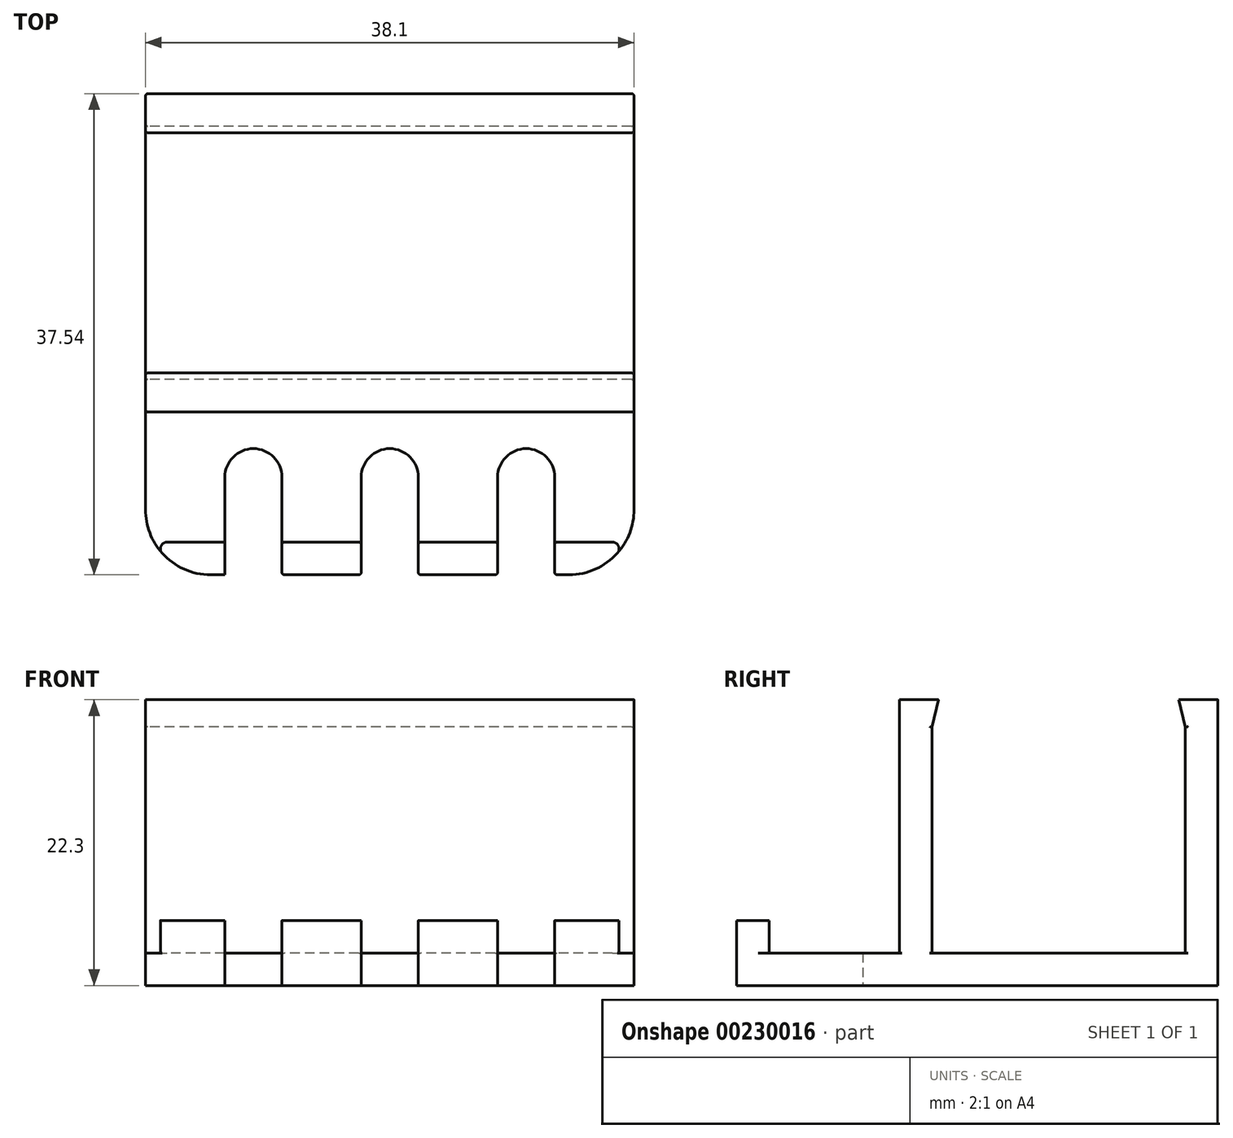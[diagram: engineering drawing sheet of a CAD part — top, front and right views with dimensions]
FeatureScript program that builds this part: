
annotation { "Feature Type Name" : "Feature", "Feature Type Description" : "" }
export const myFeature = defineFeature(function(context is Context, id is Id, definition is map)
    precondition{}
    {
        {
            var Q0;
            Q0=qCreatedBy(makeId("Right.planeOp"),FACE);
            var sketch = newSketch(context, id + "F0", { "sketchPlane" : qUnion([Q0])});
            skLineSegment(sketch, "E0.bottom", {"start": v(0, 0) * mm, "end": v(2.54, 0) * mm});
            skLineSegment(sketch, "E0.top", {"start": v(0, 22.3) * mm, "end": v(2.54, 22.3) * mm});
            skLineSegment(sketch, "E0.left", {"start": v(0, 2.54) * mm, "end": v(0, 22.3) * mm});
            skLineSegment(sketch, "E0.right", {"start": v(2.54, 2.54) * mm, "end": v(2.54, 22.3) * mm});
            skLineSegment(sketch, "E1.bottom", {"start": v(2.54, 0) * mm, "end": v(24.84, 0) * mm});
            skLineSegment(sketch, "E1.top", {"start": v(2.54, 2.54) * mm, "end": v(22.3, 2.54) * mm});
            skLineSegment(sketch, "E2.top", {"start": v(24.84, 22.3) * mm, "end": v(22.3, 22.3) * mm});
            skLineSegment(sketch, "E2.left", {"start": v(24.84, 2.54) * mm, "end": v(24.84, 22.3) * mm});
            skLineSegment(sketch, "E2.right", {"start": v(22.3, 2.54) * mm, "end": v(22.3, 20.17) * mm});
            skLineSegment(sketch, "E3.bottom", {"start": v(0, 2.54) * mm, "end": v(-12.7, 2.54) * mm});
            skLineSegment(sketch, "E3.top", {"start": v(0, 0) * mm, "end": v(-12.7, 0) * mm});
            skLineSegment(sketch, "E3.right", {"start": v(-12.7, 2.54) * mm, "end": v(-12.7, 0) * mm});
            skLineSegment(sketch, "E4", {"start": v(24.84, 2.54) * mm, "end": v(24.84, 0) * mm});
            skLineSegment(sketch, "E5", {"start": v(22.3, 20.17) * mm, "end": v(21.8, 22.3) * mm});
            skLineSegment(sketch, "E6", {"start": v(21.8, 22.3) * mm, "end": v(22.3, 22.3) * mm});
            skLineSegment(sketch, "E7", {"start": v(12.42, 2.54) * mm, "end": v(12.42, 18.7) * mm, "construction": true});
            skLineSegment(sketch, "E8.MirrorCS", {"start": v(2.54, 20.17) * mm, "end": v(3.05, 22.3) * mm});
            skLineSegment(sketch, "E9.MirrorCS", {"start": v(3.05, 22.3) * mm, "end": v(2.54, 22.3) * mm});
            skLineSegment(sketch, "E10.bottom", {"start": v(-12.7, 2.54) * mm, "end": v(-10.16, 2.54) * mm});
            skLineSegment(sketch, "E10.top", {"start": v(-12.7, 5.08) * mm, "end": v(-10.16, 5.08) * mm});
            skLineSegment(sketch, "E10.left", {"start": v(-12.7, 2.54) * mm, "end": v(-12.7, 5.08) * mm});
            skLineSegment(sketch, "E10.right", {"start": v(-10.16, 2.54) * mm, "end": v(-10.16, 5.08) * mm});
            skSolve(sketch);
        }
        {
            var Q0;
            Q0 = qSketchRegion(id + "F0", true);
            extrude(context, id + "F1", {"entities" : qUnion([Q0]), "endBound" : BoundingType.SYMMETRIC, "depth" : 38.1 * mm});
        }
        {
            var Q0;
            Q0=makeQuery(id+"F1.opExtrude","SWEPT_FACE",FACE,{"disambiguationData":[OSD([sQuery(id+"F0.wireOp",EDGE,"E3.bottom")])]});
            var sketch = newSketch(context, id + "F2", { "sketchPlane" : qUnion([Q0])});
            skLineSegment(sketch, "E11", {"start": v(-19.05, -5.08) * mm, "end": v(-12.86, -5.08) * mm, "construction": true});
            skArc(sketch, "E12", {"start": v(2.22, -5.08) * mm, "mid": v(0, -2.86) * mm, "end": v(-2.22, -5.08) * mm});
            skArc(sketch, "E13", {"start": v(12.86, -5.08) * mm, "mid": v(10.64, -2.86) * mm, "end": v(8.41, -5.08) * mm});
            skArc(sketch, "E14", {"start": v(-8.41, -5.08) * mm, "mid": v(-10.64, -2.86) * mm, "end": v(-12.86, -5.08) * mm});
            skLineSegment(sketch, "E15.top", {"start": v(-12.86, -12.7) * mm, "end": v(-8.41, -12.7) * mm});
            skLineSegment(sketch, "E15.left", {"start": v(-12.86, -5.08) * mm, "end": v(-12.86, -12.7) * mm});
            skLineSegment(sketch, "E15.right", {"start": v(-8.41, -5.08) * mm, "end": v(-8.41, -12.7) * mm});
            skLineSegment(sketch, "E16.top", {"start": v(-2.22, -12.7) * mm, "end": v(2.22, -12.7) * mm});
            skLineSegment(sketch, "E16.left", {"start": v(-2.22, -5.08) * mm, "end": v(-2.22, -12.7) * mm});
            skLineSegment(sketch, "E16.right", {"start": v(2.22, -5.08) * mm, "end": v(2.22, -12.7) * mm});
            skLineSegment(sketch, "E17.top", {"start": v(8.41, -12.7) * mm, "end": v(12.86, -12.7) * mm});
            skLineSegment(sketch, "E17.left", {"start": v(8.41, -5.08) * mm, "end": v(8.41, -12.7) * mm});
            skLineSegment(sketch, "E17.right", {"start": v(12.86, -5.08) * mm, "end": v(12.86, -12.7) * mm});
            skLineSegment(sketch, "E18.trimOffspring", {"start": v(-8.41, -5.08) * mm, "end": v(-2.22, -5.08) * mm, "construction": true});
            skLineSegment(sketch, "E19.trimOffspring", {"start": v(2.22, -5.08) * mm, "end": v(8.41, -5.08) * mm, "construction": true});
            skLineSegment(sketch, "E20.trimOffspring", {"start": v(12.86, -5.08) * mm, "end": v(19.05, -5.08) * mm, "construction": true});
            skSolve(sketch);
        }
        {
            var Q0;
            Q0 = qSketchRegion(id + "F2", true);
            extrude(context, id + "F3", {"entities" : qUnion([Q0]), "operationType" : NewBodyOperationType.REMOVE, "endBound" : BoundingType.SYMMETRIC, "depth" : 25.4 * mm});
        }
        {
            var Q0;
            Q0=makeQuery(id+"F1.opExtrude","CAP_EDGE",EDGE,{"disambiguationData":[OSD([sQuery(id+"F0.wireOp",EDGE,"E3.right"),sQuery(id+"F0.wireOp",EDGE,"E10.left")])],"isStart":false});
            var Q1;
            Q1=makeQuery(id+"F1.opExtrude","CAP_EDGE",EDGE,{"disambiguationData":[OSD([sQuery(id+"F0.wireOp",EDGE,"E3.right"),sQuery(id+"F0.wireOp",EDGE,"E10.left")])],"isStart":true});
            fillet(context, id + "F4", {"entities" : qUnion([Q0, Q1]), "radius" : 5.08 * mm, "tangentPropagation" : true, "allowEdgeOverflow" : false});
        }
        {
            var Q0;
            {var subQ0=sQuery(id+"F0.wireOp",EDGE,"E10.right");var subQ1=sQuery(id+"F0.wireOp",EDGE,"E10.left");var subQ3=sQuery(id+"F0.wireOp",EDGE,"E3.right");Q0=makeQuery(id+"F4.opFillet","BLEND_EDGE",EDGE,{"blendedFrom":[makeQuery(id+"F1.opExtrude","CAP_EDGE",EDGE,{"disambiguationData":[OSD([subQ3,subQ1])],"isStart":true}),makeQuery(id+"F3.boolean.opBoolean","SPLIT",FACE,{"disambiguationData":[TD([makeQuery(id+"F3.opExtrude","SWEPT_FACE",FACE,{"disambiguationData":[OSD([sQuery(id+"F2.wireOp",EDGE,"E15.left")])]})])],"derivedFrom":makeQuery(id+"F1.opExtrude","SWEPT_FACE",FACE,{"disambiguationData":[OSD([subQ0])]})})],"blendedInto":[makeQuery(id+"F3.boolean.opBoolean","SPLIT",FACE,{"disambiguationData":[TD([makeQuery(id+"F3.opExtrude","SWEPT_FACE",FACE,{"disambiguationData":[OSD([sQuery(id+"F2.wireOp",EDGE,"E15.left")])]})])],"derivedFrom":makeQuery(id+"F1.opExtrude","SWEPT_FACE",FACE,{"disambiguationData":[OSD([subQ0])]})})]});}
            var Q1;
            {var subQ0=sQuery(id+"F0.wireOp",EDGE,"E10.right");var subQ1=sQuery(id+"F0.wireOp",EDGE,"E10.left");var subQ3=sQuery(id+"F0.wireOp",EDGE,"E3.right");Q1=makeQuery(id+"F4.opFillet","BLEND_EDGE",EDGE,{"blendedFrom":[makeQuery(id+"F1.opExtrude","CAP_EDGE",EDGE,{"disambiguationData":[OSD([subQ3,subQ1])],"isStart":false}),makeQuery(id+"F3.boolean.opBoolean","SPLIT",FACE,{"disambiguationData":[TD([makeQuery(id+"F3.opExtrude","SWEPT_FACE",FACE,{"disambiguationData":[OSD([sQuery(id+"F2.wireOp",EDGE,"E17.right")])]})])],"derivedFrom":makeQuery(id+"F1.opExtrude","SWEPT_FACE",FACE,{"disambiguationData":[OSD([subQ0])]})})],"blendedInto":[makeQuery(id+"F3.boolean.opBoolean","SPLIT",FACE,{"disambiguationData":[TD([makeQuery(id+"F3.opExtrude","SWEPT_FACE",FACE,{"disambiguationData":[OSD([sQuery(id+"F2.wireOp",EDGE,"E17.right")])]})])],"derivedFrom":makeQuery(id+"F1.opExtrude","SWEPT_FACE",FACE,{"disambiguationData":[OSD([subQ0])]})})]});}
            fillet(context, id + "F5", {"entities" : qUnion([Q0, Q1]), "radius" : 0.5 * mm, "tangentPropagation" : true, "allowEdgeOverflow" : false});
        }
        {
            var Q0;
            Q0=makeQuery(id+"F3.boolean.opBoolean","COPY",EDGE,{"derivedFrom":makeQuery(id+"F3.opExtrude","SWEPT_EDGE",EDGE,{"disambiguationData":[OSD([sQuery(id+"F2.wireOp",EDGE,"E15.top"),sQuery(id+"F2.wireOp",EDGE,"E15.left")])]})});
            var Q1;
            Q1=makeQuery(id+"F3.boolean.opBoolean","COPY",EDGE,{"derivedFrom":makeQuery(id+"F3.opExtrude","SWEPT_EDGE",EDGE,{"disambiguationData":[OSD([sQuery(id+"F2.wireOp",EDGE,"E15.top"),sQuery(id+"F2.wireOp",EDGE,"E15.right")])]})});
            var Q2;
            Q2=makeQuery(id+"F3.boolean.opBoolean","COPY",EDGE,{"derivedFrom":makeQuery(id+"F3.opExtrude","SWEPT_EDGE",EDGE,{"disambiguationData":[OSD([sQuery(id+"F2.wireOp",EDGE,"E16.top"),sQuery(id+"F2.wireOp",EDGE,"E16.left")])]})});
            var Q3;
            Q3=makeQuery(id+"F3.boolean.opBoolean","COPY",EDGE,{"derivedFrom":makeQuery(id+"F3.opExtrude","SWEPT_EDGE",EDGE,{"disambiguationData":[OSD([sQuery(id+"F2.wireOp",EDGE,"E16.top"),sQuery(id+"F2.wireOp",EDGE,"E16.right")])]})});
            var Q4;
            Q4=makeQuery(id+"F3.boolean.opBoolean","COPY",EDGE,{"derivedFrom":makeQuery(id+"F3.opExtrude","SWEPT_EDGE",EDGE,{"disambiguationData":[OSD([sQuery(id+"F2.wireOp",EDGE,"E17.top"),sQuery(id+"F2.wireOp",EDGE,"E17.left")])]})});
            var Q5;
            Q5=makeQuery(id+"F3.boolean.opBoolean","COPY",EDGE,{"derivedFrom":makeQuery(id+"F3.opExtrude","SWEPT_EDGE",EDGE,{"disambiguationData":[OSD([sQuery(id+"F2.wireOp",EDGE,"E17.top"),sQuery(id+"F2.wireOp",EDGE,"E17.right")])]})});
            var Q6;
            Q6=makeQuery(id+"F3.boolean.opBoolean","INTERSECT",EDGE,{"derivedFrom":[makeQuery(id+"F1.opExtrude","SWEPT_FACE",FACE,{"disambiguationData":[OSD([sQuery(id+"F0.wireOp",EDGE,"E10.right")])]}),makeQuery(id+"F3.opExtrude","SWEPT_FACE",FACE,{"disambiguationData":[OSD([sQuery(id+"F2.wireOp",EDGE,"E17.right")])]})]});
            var Q7;
            Q7=makeQuery(id+"F3.boolean.opBoolean","INTERSECT",EDGE,{"derivedFrom":[makeQuery(id+"F1.opExtrude","SWEPT_FACE",FACE,{"disambiguationData":[OSD([sQuery(id+"F0.wireOp",EDGE,"E10.right")])]}),makeQuery(id+"F3.opExtrude","SWEPT_FACE",FACE,{"disambiguationData":[OSD([sQuery(id+"F2.wireOp",EDGE,"E17.left")])]})]});
            var Q8;
            Q8=makeQuery(id+"F3.boolean.opBoolean","INTERSECT",EDGE,{"derivedFrom":[makeQuery(id+"F1.opExtrude","SWEPT_FACE",FACE,{"disambiguationData":[OSD([sQuery(id+"F0.wireOp",EDGE,"E10.right")])]}),makeQuery(id+"F3.opExtrude","SWEPT_FACE",FACE,{"disambiguationData":[OSD([sQuery(id+"F2.wireOp",EDGE,"E16.right")])]})]});
            var Q9;
            Q9=makeQuery(id+"F3.boolean.opBoolean","INTERSECT",EDGE,{"derivedFrom":[makeQuery(id+"F1.opExtrude","SWEPT_FACE",FACE,{"disambiguationData":[OSD([sQuery(id+"F0.wireOp",EDGE,"E10.right")])]}),makeQuery(id+"F3.opExtrude","SWEPT_FACE",FACE,{"disambiguationData":[OSD([sQuery(id+"F2.wireOp",EDGE,"E16.left")])]})]});
            var Q10;
            Q10=makeQuery(id+"F3.boolean.opBoolean","INTERSECT",EDGE,{"derivedFrom":[makeQuery(id+"F1.opExtrude","SWEPT_FACE",FACE,{"disambiguationData":[OSD([sQuery(id+"F0.wireOp",EDGE,"E10.right")])]}),makeQuery(id+"F3.opExtrude","SWEPT_FACE",FACE,{"disambiguationData":[OSD([sQuery(id+"F2.wireOp",EDGE,"E15.right")])]})]});
            var Q11;
            Q11=makeQuery(id+"F1.opExtrude","CAP_EDGE",EDGE,{"disambiguationData":[OSD([sQuery(id+"F0.wireOp",EDGE,"E0.left")])],"isStart":false});
            var Q12;
            Q12=makeQuery(id+"F1.opExtrude","CAP_EDGE",EDGE,{"disambiguationData":[OSD([sQuery(id+"F0.wireOp",EDGE,"E0.right")])],"isStart":false});
            var Q13;
            Q13=makeQuery(id+"F1.opExtrude","CAP_EDGE",EDGE,{"disambiguationData":[OSD([sQuery(id+"F0.wireOp",EDGE,"E8.MirrorCS")])],"isStart":false});
            var Q14;
            Q14=makeQuery(id+"F1.opExtrude","CAP_EDGE",EDGE,{"disambiguationData":[OSD([sQuery(id+"F0.wireOp",EDGE,"E2.right")])],"isStart":false});
            var Q15;
            Q15=makeQuery(id+"F1.opExtrude","CAP_EDGE",EDGE,{"disambiguationData":[OSD([sQuery(id+"F0.wireOp",EDGE,"E2.left"),sQuery(id+"F0.wireOp",EDGE,"E4")])],"isStart":false});
            var Q16;
            Q16=makeQuery(id+"F1.opExtrude","CAP_EDGE",EDGE,{"disambiguationData":[OSD([sQuery(id+"F0.wireOp",EDGE,"E5")])],"isStart":false});
            var Q17;
            Q17=makeQuery(id+"F1.opExtrude","CAP_EDGE",EDGE,{"disambiguationData":[OSD([sQuery(id+"F0.wireOp",EDGE,"E0.left")])],"isStart":true});
            var Q18;
            Q18=makeQuery(id+"F1.opExtrude","CAP_EDGE",EDGE,{"disambiguationData":[OSD([sQuery(id+"F0.wireOp",EDGE,"E0.right")])],"isStart":true});
            var Q19;
            Q19=makeQuery(id+"F1.opExtrude","CAP_EDGE",EDGE,{"disambiguationData":[OSD([sQuery(id+"F0.wireOp",EDGE,"E2.right")])],"isStart":true});
            var Q20;
            Q20=makeQuery(id+"F1.opExtrude","CAP_EDGE",EDGE,{"disambiguationData":[OSD([sQuery(id+"F0.wireOp",EDGE,"E2.left"),sQuery(id+"F0.wireOp",EDGE,"E4")])],"isStart":true});
            var Q21;
            Q21=makeQuery(id+"F1.opExtrude","CAP_EDGE",EDGE,{"disambiguationData":[OSD([sQuery(id+"F0.wireOp",EDGE,"E5")])],"isStart":true});
            var Q22;
            Q22=makeQuery(id+"F1.opExtrude","CAP_EDGE",EDGE,{"disambiguationData":[OSD([sQuery(id+"F0.wireOp",EDGE,"E8.MirrorCS")])],"isStart":true});
            fillet(context, id + "F6", {"entities" : qUnion([Q0, Q1, Q2, Q3, Q4, Q5, Q6, Q7, Q8, Q9, Q10, Q11, Q12, Q13, Q14, Q15, Q16, Q17, Q18, Q19, Q20, Q21, Q22]), "radius" : .2 * mm, "tangentPropagation" : true, "allowEdgeOverflow" : false});
        }
    });
